# Revit family: Hook-BathrobeHolderSingle-Vitra-OriginSeries-A44884
name_source: partatom
category: Plumbing Fixtures
revit_build: Autodesk Revit 2017 (Build: 20160225_1515(x64)
units: mm (PartAtom-declared; Revit-internal decimal feet)

## family parameters
Cut with Voids When Loaded = No
Host = Face
OmniClass Number = 23.45.05.14.99
OmniClass Title = Other Sanitary Washing Plumbing Fixtures
Part Type = Normal
Room Calculation Point = No
Round Connector Dimension = Use Diameter
Shared = Yes

## types (4) — shared parameters
BIMobject category = Sanitary - Accessories
CW Connection = No
Depth(mm) = 64 mm  [stored 0.209974 ft]
Description = Origin Hook Bathrobe Holder
Design country = Turkey
HW Connection = No
Height(mm) = 58 mm  [stored 0.190289 ft]
IFC Classification = Furnishing Element
Manufacturer = Vitra
Manufacturer name = Vitra
Masterformat 2014 Code = 12 44 00
Masterformat 2014 Description = Bath Furnishings
MountingType = Wall-mounted
NBS Referans Code = 31-75
NBS Referans Description = Sanitary Accessories
Nominal height = 0.000
Nominal width = 0.000
OmniClass Code = 23-19 31 17
OmniClass Description = Sanitary Room Units
Product Type = Hook Bathrobe Holder
Product certification = https://vitraglobal.com
Product data url = https://www.vitraglobal.com
Product family = Origin Series
Product group = Hook Bathrobe Holder
Technical description = https://www.vitra.com.tr
UNSPSC Code = 301815
UNSPSC Description = Sanitary ware
URL = https://vitraglobal.com
Uniclass 1.4 Code = L721
Uniclass 1.4 Description = Sanitary equipment
Uniclass 2.0 Code = PR-31-75
Uniclass 2.0 Description = Sanitary Accessories
Uniclass 2015 Code = Pr_40_20_76
Uniclass 2015 Name = Sanitary accessories
Uniformat II Code = E20
Uniformat II Description = FURNISHINGS
Vent Connection = No
Warranty Period (Year) = 5 years
Waste Connection = No
Weight Net (kg) = 0,250
Width(mm) = 58 mm  [stored 0.190289 ft]
Youtube = https://www.youtube.com
zero-valued in all types: CWFU, Cost, Default Elevation, HWFU, WFU

## per-type parameters (varying)
| type | Article No. (default) | Coating Material | Color | Model | Product SKU |
| Hook-BathrobeHolder-Vitra-OriginSeries(Chrome)-A44884 | A44884 | Vitra-Chrome | Chrome | A44884 | A44884 |
| Hook-BathrobeHolder-Vitra-OriginSeries(Copper)-A4488426 | A4488426 | Vitra-Copper | Copper | A4488426 | A4488426 |
| Hook-BathrobeHolder-Vitra-OriginSeries(BrushedNickel)-A4488434 | A4488434 | Vitra-BrushedNickel | Brushed Nickel | A4488434 | A4488434 |
| Hook-BathrobeHolder-Vitra-OriginSeries(Black)-A4488436 | A4488436 | Vitra-Black | Black | A4488436 | A4488436 |

note: [stored X ft] marks values corroborated as IEEE doubles in the binary element streams (Revit-internal decimal feet)

## geometry (parser evidence)
native form markers: Sweep x3
no freeform markers — native parametric forms only
